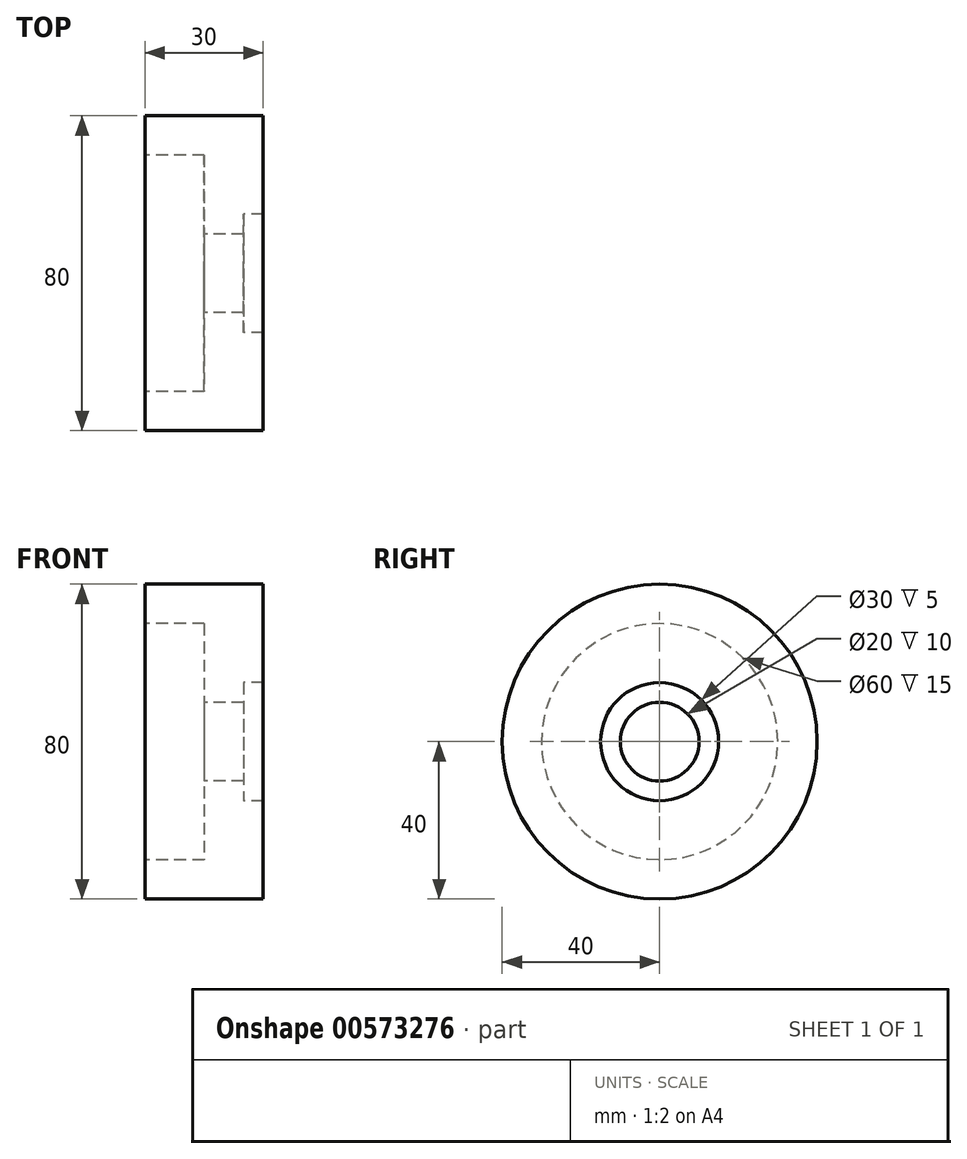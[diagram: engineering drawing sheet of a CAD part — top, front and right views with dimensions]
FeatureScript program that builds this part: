
annotation { "Feature Type Name" : "Feature", "Feature Type Description" : "" }
export const myFeature = defineFeature(function(context is Context, id is Id, definition is map)
    precondition{}
    {
        {
            var Q0;
            Q0=qCreatedBy(makeId("Front.planeOp"),FACE);
            var sketch = newSketch(context, id + "F0", { "sketchPlane" : qUnion([Q0])});
            skLineSegment(sketch, "E0", {"start": v(-53.93, 0) * mm, "end": v(56.43, 0) * mm, "construction": true});
            skLineSegment(sketch, "E1", {"start": v(-30, -40) * mm, "end": v(0, -40) * mm});
            skLineSegment(sketch, "E2", {"start": v(0, -40) * mm, "end": v(0, -15) * mm});
            skLineSegment(sketch, "E3", {"start": v(0, -15) * mm, "end": v(-5, -15) * mm});
            skLineSegment(sketch, "E4", {"start": v(-5, -15) * mm, "end": v(-5, -10) * mm});
            skLineSegment(sketch, "E5", {"start": v(-5, -10) * mm, "end": v(-15, -10) * mm});
            skLineSegment(sketch, "E6", {"start": v(-15, -10) * mm, "end": v(-15, -30) * mm});
            skLineSegment(sketch, "E7", {"start": v(-15, -30) * mm, "end": v(-30, -30) * mm});
            skLineSegment(sketch, "E8", {"start": v(-30, -30) * mm, "end": v(-30, -40) * mm});
            skSolve(sketch);
        }
        {
            var Q0;
            Q0=makeQuery(id+"F0.imprint","IMPRINT",FACE,{"disambiguationData":[TD([[makeQuery(id+"F0.imprint","IMPRINT",EDGE,{"derivedFrom":sQuery(id+"F0.wireOp",EDGE,"E1")}),1.0]])]});
            var Q1;
            Q1=sQuery(id+"F0.wireOp",EDGE,"E0");
            revolve(context, id + "F1", {"entities" : qUnion([Q0]), "axis" : qUnion([Q1]), "revolveType" : RevolveType.FULL});
        }
    });
